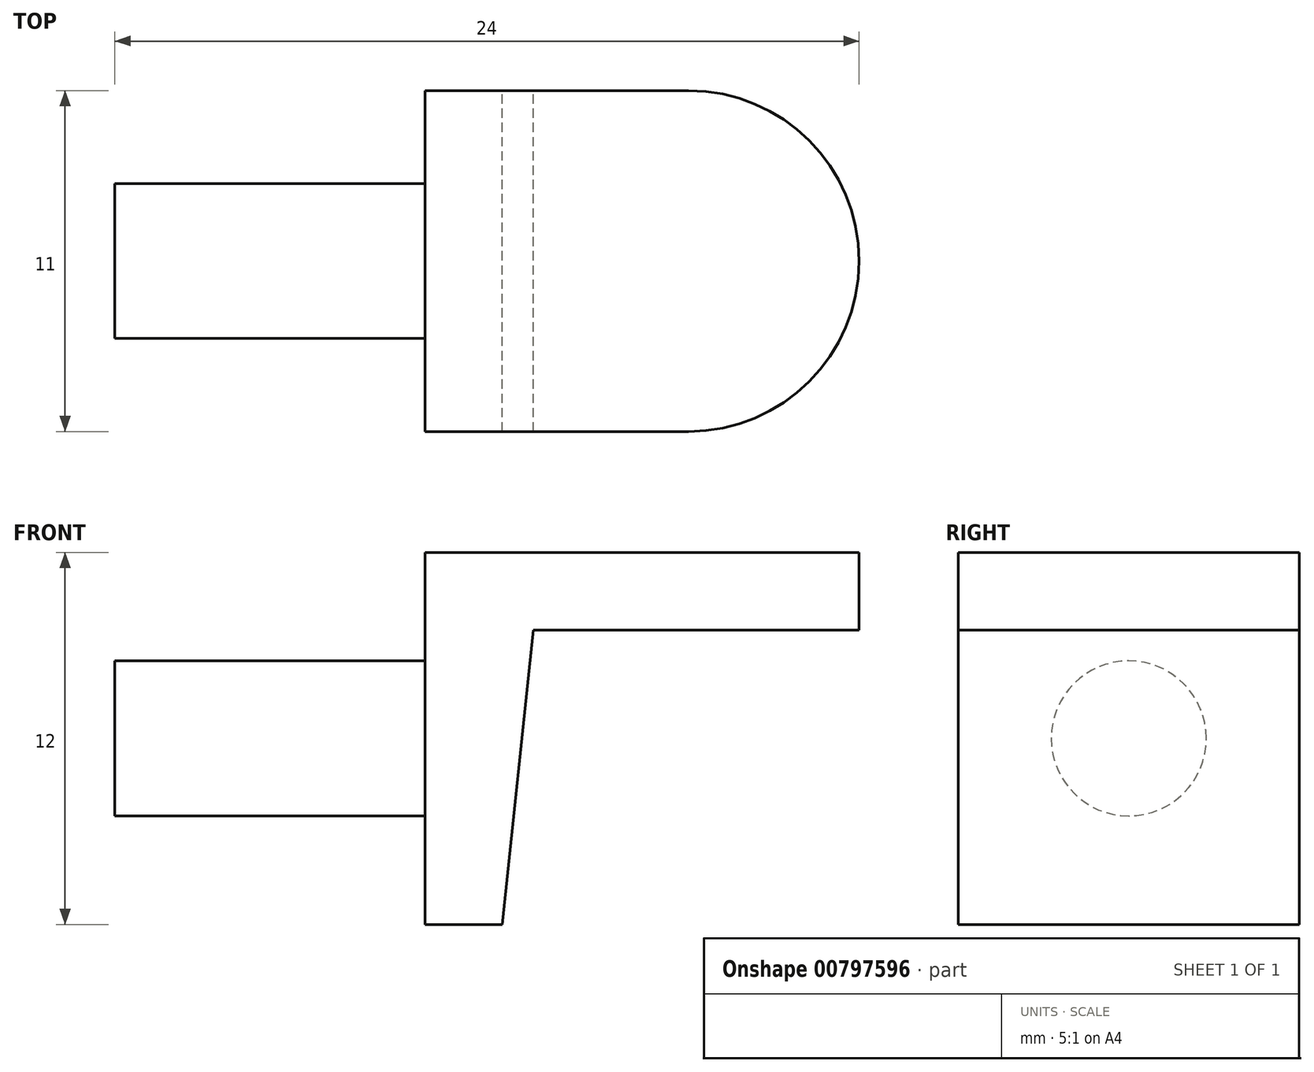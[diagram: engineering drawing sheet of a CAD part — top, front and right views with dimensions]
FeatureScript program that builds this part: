
annotation { "Feature Type Name" : "Feature", "Feature Type Description" : "" }
export const myFeature = defineFeature(function(context is Context, id is Id, definition is map)
    precondition{}
    {
        {
            var Q0;
            Q0=qCreatedBy(makeId("Front.planeOp"),FACE);
            var sketch = newSketch(context, id + "F0", { "sketchPlane" : qUnion([Q0])});
            skLineSegment(sketch, "E0", {"start": v(0, 0) * mm, "end": v(14, 0) * mm});
            skLineSegment(sketch, "E1", {"start": v(14, 0) * mm, "end": v(14, -2.5) * mm});
            skLineSegment(sketch, "E2", {"start": v(14, -2.5) * mm, "end": v(3.5, -2.5) * mm});
            skLineSegment(sketch, "E3", {"start": v(3.5, -2.5) * mm, "end": v(2.5, -12) * mm});
            skLineSegment(sketch, "E4", {"start": v(2.5, -12) * mm, "end": v(0, -12) * mm});
            skLineSegment(sketch, "E5", {"start": v(0, -12) * mm, "end": v(0, 0) * mm});
            skSolve(sketch);
        }
        {
            var Q0;
            Q0=makeQuery(id+"F0.imprint","IMPRINT",FACE,{"disambiguationData":[TD([[makeQuery(id+"F0.imprint","IMPRINT",EDGE,{"derivedFrom":sQuery(id+"F0.wireOp",EDGE,"E0")}),-1.0]])]});
            extrude(context, id + "F1", {"entities" : qUnion([Q0]), "depth" : 11 * mm, "offsetDistance" : 25 * mm});
        }
        {
            var Q0;
            Q0=makeQuery(id+"F1.opExtrude","SWEPT_BODY",BODY,{"disambiguationData":[OSD([sQuery(id+"F0.wireOp",EDGE,"E0"),sQuery(id+"F0.wireOp",EDGE,"E1"),sQuery(id+"F0.wireOp",EDGE,"E2"),sQuery(id+"F0.wireOp",EDGE,"E3"),sQuery(id+"F0.wireOp",EDGE,"E4"),sQuery(id+"F0.wireOp",EDGE,"E5")])]});
            var Q1;
            Q1=makeQuery(id+"F1.opExtrude","SWEPT_EDGE",EDGE,{"disambiguationData":[OSD([sQuery(id+"F0.wireOp",EDGE,"E0"),sQuery(id+"F0.wireOp",EDGE,"E5")])]});
            transform(context, id + "F2", {"entities" : qUnion([Q0]), "transformType" : TransformType.TRANSLATION_DISTANCE, "transformDirection" : qUnion([Q1]), "distance" : 5.5 * mm, "makeCopy" : false});
        }
        {
            var Q0;
            Q0=makeQuery(id+"F1.opExtrude","SWEPT_FACE",FACE,{"disambiguationData":[OSD([sQuery(id+"F0.wireOp",EDGE,"E0")])]});
            var sketch = newSketch(context, id + "F3", { "sketchPlane" : qUnion([Q0])});
            skArc(sketch, "E6", {"start": v(8.5, -5.5) * mm, "mid": v(14, 0) * mm, "end": v(8.5, 5.5) * mm});
            skSolve(sketch);
        }
        {
            var Q0;
            {var subQ0=sQuery(id+"F3.wireOp",EDGE,"E6");var subQ1=sQuery(id+"F0.wireOp",EDGE,"E0");var subQ2=makeQuery(id+"F1.opExtrude","CAP_EDGE",EDGE,{"disambiguationData":[OSD([subQ1])],"isStart":true});var subQ3=makeQuery(id+"F3.imprint","INTERSECT",VERTEX,{"derivedFrom":[subQ2,subQ0]});Q0=makeQuery(id+"F3.imprint","IMPRINT",FACE,{"disambiguationData":[TD([[makeQuery(id+"F3.imprint","IMPRINT",EDGE,{"disambiguationData":[TD([[subQ3,1.0]])],"derivedFrom":subQ0}),-1.0]])]});}
            var Q1;
            {var subQ0=sQuery(id+"F3.wireOp",EDGE,"E6");var subQ1=sQuery(id+"F0.wireOp",EDGE,"E0");var subQ2=makeQuery(id+"F1.opExtrude","CAP_EDGE",EDGE,{"disambiguationData":[OSD([subQ1])],"isStart":false});var subQ3=makeQuery(id+"F3.imprint","INTERSECT",VERTEX,{"derivedFrom":[subQ2,subQ0]});Q1=makeQuery(id+"F3.imprint","IMPRINT",FACE,{"disambiguationData":[TD([[makeQuery(id+"F3.imprint","IMPRINT",EDGE,{"disambiguationData":[TD([[subQ3,-1.0]])],"derivedFrom":subQ0}),-1.0]])]});}
            extrude(context, id + "F4", {"entities" : qUnion([Q0, Q1]), "operationType" : NewBodyOperationType.REMOVE, "endBound" : BoundingType.THROUGH_ALL, "oppositeDirection" : true, "depth" : 25 * mm, "offsetDistance" : 25 * mm});
        }
        {
            var Q0;
            Q0=makeQuery(id+"F1.opExtrude","SWEPT_FACE",FACE,{"disambiguationData":[OSD([sQuery(id+"F0.wireOp",EDGE,"E5")])]});
            var sketch = newSketch(context, id + "F5", { "sketchPlane" : qUnion([Q0])});
            skCircle(sketch, "E7", {"center": v(0, -6) * mm, "radius": 2.5 * mm});
            skSolve(sketch);
        }
        {
            var Q0;
            Q0=makeQuery(id+"F5.imprint","IMPRINT",FACE,{"disambiguationData":[TD([[makeQuery(id+"F5.imprint","IMPRINT",EDGE,{"derivedFrom":sQuery(id+"F5.wireOp",EDGE,"E7")}),1.0]])]});
            extrude(context, id + "F6", {"entities" : qUnion([Q0]), "operationType" : NewBodyOperationType.ADD, "depth" : 10 * mm, "offsetDistance" : 25 * mm});
        }
    });
